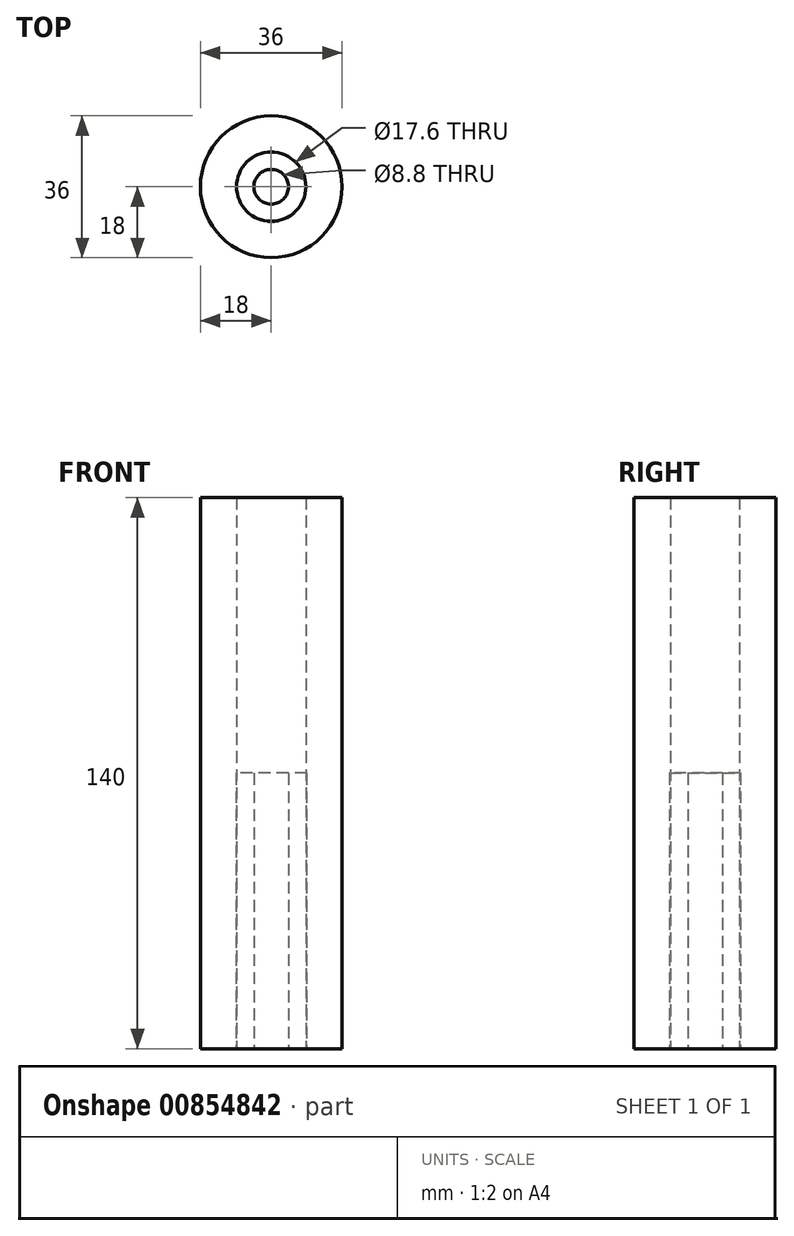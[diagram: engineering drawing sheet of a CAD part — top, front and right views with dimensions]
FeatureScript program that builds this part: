
annotation { "Feature Type Name" : "Feature", "Feature Type Description" : "" }
export const myFeature = defineFeature(function(context is Context, id is Id, definition is map)
    precondition{}
    {
        {
            var Q0;
            Q0=qCreatedBy(makeId("Top.planeOp"),FACE);
            var sketch = newSketch(context, id + "F0", { "sketchPlane" : qUnion([Q0])});
            skCircle(sketch, "E0", {"center": v(0, 0) * mm, "radius": 9 * mm});
            skCircle(sketch, "E1", {"center": v(0, 0) * mm, "radius": 4.4 * mm});
            skSolve(sketch);
        }
        {
            var Q0;
            Q0 = qSketchRegion(id + "F0", true);
            extrude(context, id + "F1", {"entities" : qUnion([Q0]), "depth" : 70 * mm, "offsetDistance" : 25 * mm});
        }
        {
            var Q0;
            Q0=makeQuery(id+"F1.opExtrude","SWEPT_BODY",BODY,{"disambiguationData":[OSD([sQuery(id+"F0.wireOp",EDGE,"E0"),sQuery(id+"F0.wireOp",EDGE,"E1")])]});
            var Q1;
            Q1=qCreatedBy(makeId("Origin.pointOp"),VERTEX);
            transform(context, id + "F2", {"entities" : qUnion([Q0]), "transformType" : TransformType.SCALE_UNIFORMLY, "scale" : 2, "scalePoint" : qUnion([Q1]), "makeCopy" : true});
        }
    });
